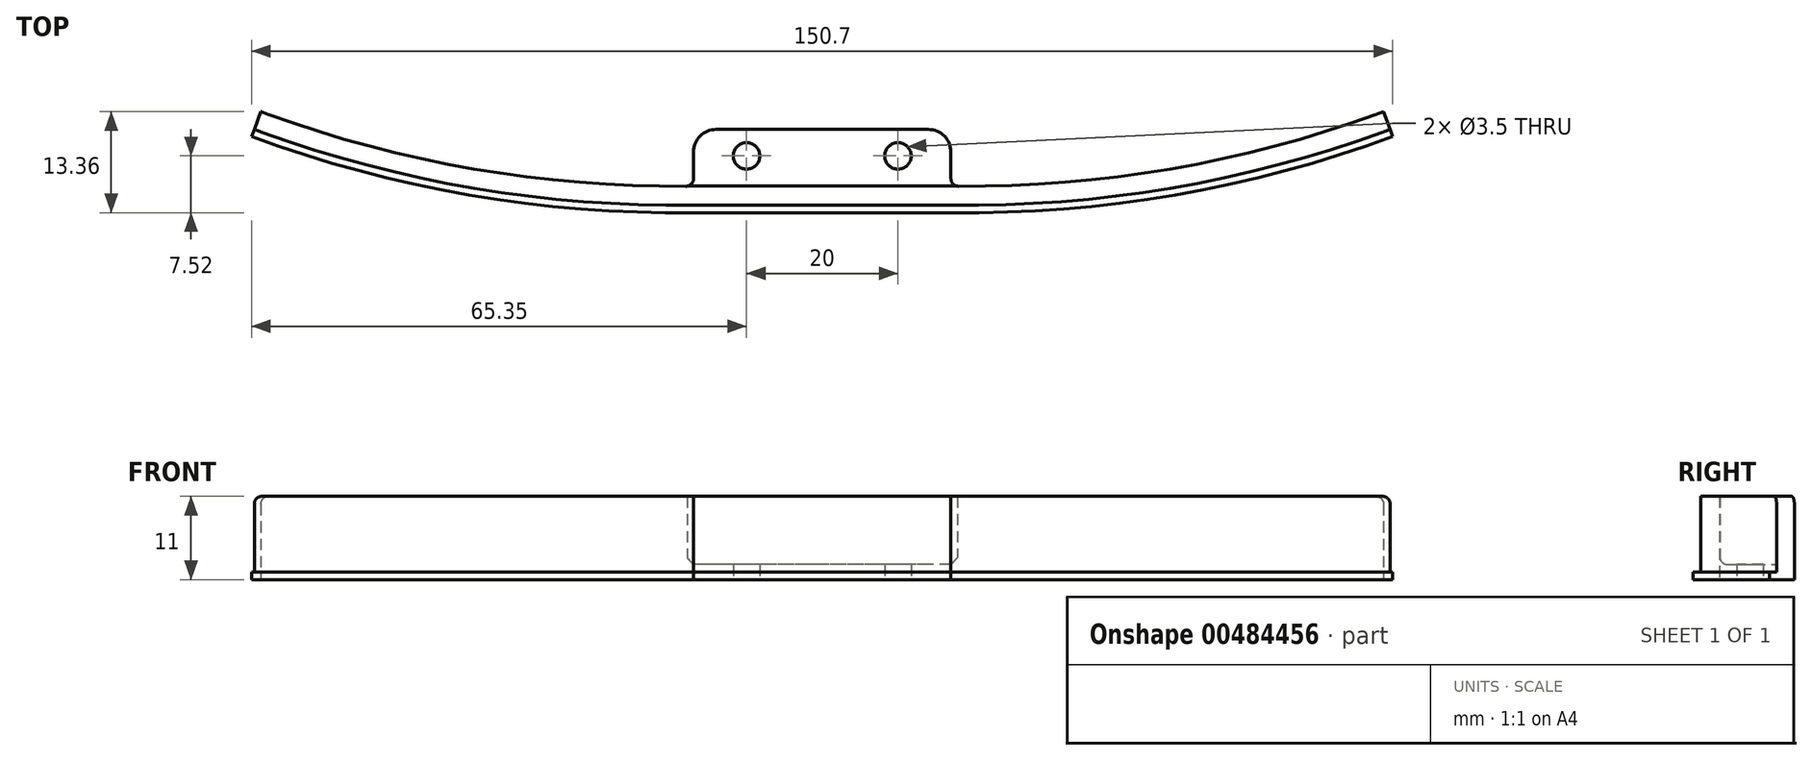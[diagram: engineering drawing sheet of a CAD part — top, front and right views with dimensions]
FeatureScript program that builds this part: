
annotation { "Feature Type Name" : "Feature", "Feature Type Description" : "" }
export const myFeature = defineFeature(function(context is Context, id is Id, definition is map)
    precondition{}
    {
        {
            var Q0;
            Q0=qCreatedBy(makeId("Top.planeOp"),FACE);
            var sketch = newSketch(context, id + "F0", { "sketchPlane" : qUnion([Q0])});
            skLineSegment(sketch, "E0.bottom", {"start": v(-17, 5) * mm, "end": v(17, 5) * mm});
            skLineSegment(sketch, "E0.top", {"start": v(-17, -5) * mm, "end": v(17, -5) * mm, "construction": true});
            skLineSegment(sketch, "E0.left", {"start": v(-17, 5) * mm, "end": v(-17, -2.5) * mm});
            skLineSegment(sketch, "E0.right", {"start": v(17, 5) * mm, "end": v(17, -2.5) * mm});
            skLineSegment(sketch, "E1", {"start": v(-17, 5) * mm, "end": v(-75, 5) * mm, "construction": true});
            skLineSegment(sketch, "E2", {"start": v(17, 5) * mm, "end": v(75, 5) * mm, "construction": true});
            skArc(sketch, "E3", {"start": v(-75, 5) * mm, "mid": v(-46.46, -2.69) * mm, "end": v(-17, -5) * mm, "construction": true});
            skArc(sketch, "E4", {"start": v(17, -5) * mm, "mid": v(46.46, -2.69) * mm, "end": v(75, 5) * mm, "construction": true});
            skArc(sketch, "E5.0", {"start": v(-74.13, 7.34) * mm, "mid": v(-46.02, -0.23) * mm, "end": v(-17, -2.5) * mm});
            skArc(sketch, "E6.0", {"start": v(17, -2.5) * mm, "mid": v(46.02, -0.23) * mm, "end": v(74.13, 7.34) * mm});
            skLineSegment(sketch, "E7", {"start": v(-74.13, 7.34) * mm, "end": v(-75.35, 4.06) * mm});
            skLineSegment(sketch, "E8", {"start": v(74.13, 7.34) * mm, "end": v(75.35, 4.06) * mm});
            skCircle(sketch, "E9", {"center": v(-10, 1.5) * mm, "radius": 1.75 * mm});
            skCircle(sketch, "E10", {"center": v(10, 1.5) * mm, "radius": 1.75 * mm});
            skArc(sketch, "E11.0", {"start": v(17, -6) * mm, "mid": v(46.64, -3.67) * mm, "end": v(75.35, 4.06) * mm});
            skLineSegment(sketch, "E11.1", {"start": v(-17, -6) * mm, "end": v(17, -6) * mm});
            skArc(sketch, "E11.2", {"start": v(-75.35, 4.06) * mm, "mid": v(-46.64, -3.67) * mm, "end": v(-17, -6) * mm});
            skSolve(sketch);
        }
        {
            var Q0;
            Q0 = qSketchRegion(id + "F0", true);
            extrude(context, id + "F1", {"entities" : qUnion([Q0]), "depth" : 11 * mm});
        }
        {
            var Q0;
            Q0=makeQuery(id+"F1.opExtrude","SWEPT_FACE",FACE,{"disambiguationData":[OSD([sQuery(id+"F0.wireOp",EDGE,"E0.left")])]});
            var sketch = newSketch(context, id + "F2", { "sketchPlane" : qUnion([Q0])});
            skLineSegment(sketch, "E12.bottom", {"start": v(2.5, 11) * mm, "end": v(-5, 11) * mm});
            skLineSegment(sketch, "E12.top", {"start": v(2.5, 2) * mm, "end": v(-5, 2) * mm});
            skLineSegment(sketch, "E12.left", {"start": v(2.5, 11) * mm, "end": v(2.5, 2) * mm});
            skLineSegment(sketch, "E12.right", {"start": v(-5, 11) * mm, "end": v(-5, 2) * mm});
            skSolve(sketch);
        }
        {
            var Q0;
            Q0 = qSketchRegion(id + "F2", true);
            extrude(context, id + "F3", {"entities" : qUnion([Q0]), "operationType" : NewBodyOperationType.REMOVE, "oppositeDirection" : true, "depth" : 34 * mm});
        }
        {
            var Q0;
            Q0=makeQuery(id+"F3.boolean.opBoolean","SPLIT",EDGE,{"derivedFrom":makeQuery(id+"F1.opExtrude","SWEPT_EDGE",EDGE,{"disambiguationData":[OSD([sQuery(id+"F0.wireOp",EDGE,"E0.left"),sQuery(id+"F0.wireOp",EDGE,"E5.0")])]})});
            var Q1;
            Q1=makeQuery(id+"F3.boolean.opBoolean","COPY",EDGE,{"derivedFrom":makeQuery(id+"F3.opExtrude","SWEPT_EDGE",EDGE,{"disambiguationData":[OSD([sQuery(id+"F0.wireOp",EDGE,"E0.left"),sQuery(id+"F0.wireOp",EDGE,"E5.0"),sQuery(id+"F2.wireOp",EDGE,"E12.top"),sQuery(id+"F2.wireOp",EDGE,"E12.left")])]})});
            var Q2;
            Q2=makeQuery(id+"F3.boolean.opBoolean","SPLIT",EDGE,{"derivedFrom":makeQuery(id+"F1.opExtrude","SWEPT_EDGE",EDGE,{"disambiguationData":[OSD([sQuery(id+"F0.wireOp",EDGE,"E0.right"),sQuery(id+"F0.wireOp",EDGE,"E6.0")])]})});
            fillet(context, id + "F4", {"entities" : qUnion([Q0, Q1, Q2]), "radius" : 1 * mm, "tangentPropagation" : true, "allowEdgeOverflow" : false});
        }
        {
            var Q0;
            Q0=makeQuery(id+"F1.opExtrude","SWEPT_EDGE",EDGE,{"disambiguationData":[OSD([sQuery(id+"F0.wireOp",EDGE,"E0.bottom"),sQuery(id+"F0.wireOp",EDGE,"E0.left")])]});
            var Q1;
            Q1=makeQuery(id+"F1.opExtrude","SWEPT_EDGE",EDGE,{"disambiguationData":[OSD([sQuery(id+"F0.wireOp",EDGE,"E0.bottom"),sQuery(id+"F0.wireOp",EDGE,"E0.right")])]});
            fillet(context, id + "F5", {"entities" : qUnion([Q0, Q1]), "radius" : 3 * mm, "tangentPropagation" : true, "allowEdgeOverflow" : false});
        }
        {
            var Q0;
            Q0=makeQuery(id+"F1.opExtrude","CAP_EDGE",EDGE,{"disambiguationData":[OSD([sQuery(id+"F0.wireOp",EDGE,"E7")])],"isStart":false});
            var Q1;
            Q1=makeQuery(id+"F1.opExtrude","CAP_EDGE",EDGE,{"disambiguationData":[OSD([sQuery(id+"F0.wireOp",EDGE,"E8")])],"isStart":false});
            fillet(context, id + "F6", {"entities" : qUnion([Q0, Q1]), "radius" : 1 * mm, "tangentPropagation" : true, "allowEdgeOverflow" : false});
        }
        {
            var Q0;
            Q0=makeQuery(id+"F1.opExtrude","CAP_FACE",FACE,{"disambiguationData":[OSD([sQuery(id+"F0.wireOp",EDGE,"E0.bottom"),sQuery(id+"F0.wireOp",EDGE,"E0.left"),sQuery(id+"F0.wireOp",EDGE,"E0.right"),sQuery(id+"F0.wireOp",EDGE,"E5.0"),sQuery(id+"F0.wireOp",EDGE,"E6.0"),sQuery(id+"F0.wireOp",EDGE,"E7"),sQuery(id+"F0.wireOp",EDGE,"E8"),sQuery(id+"F0.wireOp",EDGE,"E9"),sQuery(id+"F0.wireOp",EDGE,"E10"),sQuery(id+"F0.wireOp",EDGE,"E11.0"),sQuery(id+"F0.wireOp",EDGE,"E11.1"),sQuery(id+"F0.wireOp",EDGE,"E11.2")])],"isStart":false});
            var sketch = newSketch(context, id + "F7", { "sketchPlane" : qUnion([Q0])});
            skLineSegment(sketch, "E13.bottom", {"start": v(-17, 5) * mm, "end": v(17, 5) * mm, "construction": true});
            skLineSegment(sketch, "E13.top", {"start": v(-17, -5) * mm, "end": v(17, -5) * mm});
            skLineSegment(sketch, "E13.left", {"start": v(-17, 5) * mm, "end": v(-17, -3) * mm, "construction": true});
            skLineSegment(sketch, "E13.right", {"start": v(17, 5) * mm, "end": v(17, -3) * mm, "construction": true});
            skLineSegment(sketch, "E14", {"start": v(-17, 5) * mm, "end": v(-75, 5) * mm, "construction": true});
            skLineSegment(sketch, "E15", {"start": v(17, 5) * mm, "end": v(75, 5) * mm, "construction": true});
            skArc(sketch, "E16", {"start": v(-75, 5) * mm, "mid": v(-46.46, -2.69) * mm, "end": v(-17, -5) * mm});
            skArc(sketch, "E17", {"start": v(17, -5) * mm, "mid": v(46.46, -2.69) * mm, "end": v(75, 5) * mm});
            skArc(sketch, "E18.0", {"start": v(-74.3, 6.87) * mm, "mid": v(-46.1, -0.72) * mm, "end": v(-17, -3) * mm, "construction": true});
            skArc(sketch, "E19.0", {"start": v(17, -3) * mm, "mid": v(46.1, -0.72) * mm, "end": v(74.3, 6.87) * mm, "construction": true});
            skLineSegment(sketch, "E20", {"start": v(-75, 5) * mm, "end": v(-75.35, 4.06) * mm});
            skLineSegment(sketch, "E21", {"start": v(75, 5) * mm, "end": v(75.35, 4.06) * mm});
            skCircle(sketch, "E22", {"center": v(-10, 1.5) * mm, "radius": 1.75 * mm, "construction": true});
            skCircle(sketch, "E23", {"center": v(10, 1.5) * mm, "radius": 1.75 * mm, "construction": true});
            skArc(sketch, "E24.0", {"start": v(17, -6) * mm, "mid": v(46.64, -3.67) * mm, "end": v(75.35, 4.06) * mm});
            skLineSegment(sketch, "E24.1", {"start": v(-17, -6) * mm, "end": v(17, -6) * mm});
            skArc(sketch, "E24.2", {"start": v(-75.35, 4.06) * mm, "mid": v(-46.64, -3.67) * mm, "end": v(-17, -6) * mm});
            skSolve(sketch);
        }
        {
            var Q0;
            Q0 = qSketchRegion(id + "F7", true);
            extrude(context, id + "F8", {"entities" : qUnion([Q0]), "operationType" : NewBodyOperationType.REMOVE, "oppositeDirection" : true, "depth" : 10 * mm});
        }
    });
